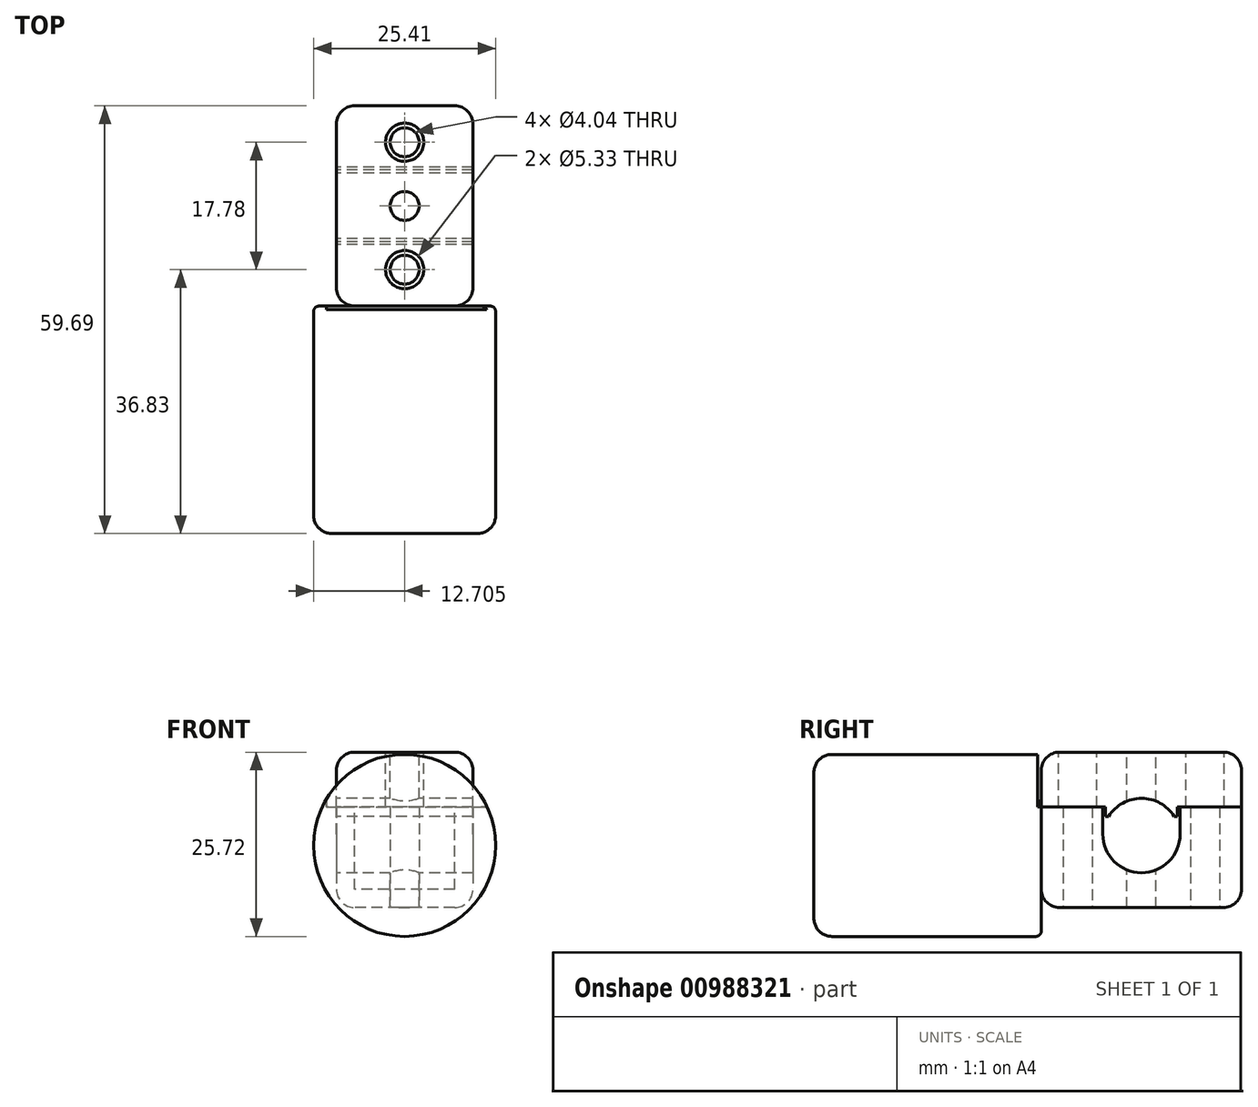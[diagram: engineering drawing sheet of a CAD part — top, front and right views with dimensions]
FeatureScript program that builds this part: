
annotation { "Feature Type Name" : "Feature", "Feature Type Description" : "" }
export const myFeature = defineFeature(function(context is Context, id is Id, definition is map)
    precondition{}
    {
        {
            var Q0;
            Q0=qCreatedBy(makeId("Right.planeOp"),FACE);
            var sketch = newSketch(context, id + "F0", { "sketchPlane" : qUnion([Q0])});
            skLineSegment(sketch, "E0", {"start": v(0, 11.43) * mm, "end": v(-13.97, 11.43) * mm});
            skLineSegment(sketch, "E1", {"start": v(-13.97, -10.27) * mm, "end": v(0, -10.27) * mm});
            skLineSegment(sketch, "E2", {"start": v(13.97, 3.81) * mm, "end": v(13.97, 11.43) * mm});
            skLineSegment(sketch, "E3", {"start": v(0, 11.43) * mm, "end": v(13.97, 11.43) * mm});
            skLineSegment(sketch, "E4", {"start": v(13.97, -10.27) * mm, "end": v(0, -10.27) * mm});
            skArc(sketch, "E5.trimOffspring", {"start": v(-5.4, 0) * mm, "mid": v(0, -5.4) * mm, "end": v(5.4, 0) * mm});
            skLineSegment(sketch, "E6", {"start": v(5.4, 0) * mm, "end": v(5.4, 3.78) * mm});
            skLineSegment(sketch, "E7", {"start": v(5.4, 3.78) * mm, "end": v(13.97, 3.78) * mm});
            skLineSegment(sketch, "E8", {"start": v(13.97, 3.78) * mm, "end": v(13.97, -10.27) * mm});
            skLineSegment(sketch, "E9", {"start": v(-13.97, 3.78) * mm, "end": v(-5.4, 3.78) * mm});
            skLineSegment(sketch, "E10", {"start": v(-5.4, 3.78) * mm, "end": v(-5.4, 0) * mm});
            skLineSegment(sketch, "E11", {"start": v(-13.97, -10.27) * mm, "end": v(-13.97, 3.78) * mm});
            skLineSegment(sketch, "E12", {"start": v(-13.97, 3.81) * mm, "end": v(-13.97, 11.43) * mm});
            skLineSegment(sketch, "E13.trimOffspring", {"start": v(-13.97, 3.81) * mm, "end": v(-5.02, 3.81) * mm});
            skLineSegment(sketch, "E14.left", {"start": v(5.02, 3.81) * mm, "end": v(5.02, 2.46) * mm});
            skLineSegment(sketch, "E15.left", {"start": v(-5.02, 3.81) * mm, "end": v(-5.02, 2.46) * mm});
            skLineSegment(sketch, "E16.trimOffspring", {"start": v(5.02, 3.81) * mm, "end": v(13.97, 3.81) * mm});
            skLineSegment(sketch, "E17", {"start": v(5.02, 2.46) * mm, "end": v(4.57, 2.46) * mm});
            skLineSegment(sketch, "E18", {"start": v(-5.02, 2.46) * mm, "end": v(-4.57, 2.46) * mm});
            skArc(sketch, "E19", {"start": v(4.57, 2.46) * mm, "mid": v(0, 4.98) * mm, "end": v(-4.57, 2.46) * mm});
            skSolve(sketch);
        }
        {
            var Q0;
            Q0=qSketchRegion(id+"F0",true);
            extrude(context, id + "F1", {"entities" : qUnion([Q0]), "depth" : 19.05 * mm, "offsetDistance" : 25.4 * mm});
        }
        {
            var Q0;
            Q0=makeQuery(id+"F1.opExtrude","SWEPT_FACE",FACE,{"disambiguationData":[OSD([sQuery(id+"F0.wireOp",EDGE,"E0"),sQuery(id+"F0.wireOp",EDGE,"E3")])]});
            var sketch = newSketch(context, id + "F2", { "sketchPlane" : qUnion([Q0])});
            skCircle(sketch, "E20", {"center": v(9.53, -8.9) * mm, "radius": 2.67 * mm});
            skPoint(sketch, "E20.centerSnap0", {"position": v(9.53, 13.97) * mm});
            skCircle(sketch, "E21", {"center": v(9.53, 8.9) * mm, "radius": 2.67 * mm});
            skCircle(sketch, "E22", {"center": v(9.53, 0) * mm, "radius": 2.02 * mm});
            skSolve(sketch);
        }
        {
            var Q0;
            Q0=qSketchRegion(id+"F2",true);
            extrude(context, id + "F3", {"entities" : qUnion([Q0]), "operationType" : NewBodyOperationType.REMOVE, "oppositeDirection" : true, "depth" : 25.4 * mm, "offsetDistance" : 25.4 * mm});
        }
        {
            var Q0;
            Q0=makeQuery(id+"F1.opExtrude","SWEPT_FACE",FACE,{"disambiguationData":[OSD([sQuery(id+"F0.wireOp",EDGE,"E1"),sQuery(id+"F0.wireOp",EDGE,"E4")])]});
            var sketch = newSketch(context, id + "F4", { "sketchPlane" : qUnion([Q0])});
            skSolve(sketch);
        }
        {
            var Q0;
            Q0=makeQuery(id+"F1.opExtrude","SWEPT_EDGE",EDGE,{"disambiguationData":[OSD([sQuery(id+"F0.wireOp",EDGE,"RtNWUVL0-efdT-tvqy-NiaK-mgzKuhDWmYlO"),sQuery(id+"F0.wireOp",EDGE,"E4")])]});
            var Q1;
            Q1=makeQuery(id+"F1.opExtrude","SWEPT_EDGE",EDGE,{"disambiguationData":[OSD([sQuery(id+"F0.wireOp",EDGE,"E2"),sQuery(id+"F0.wireOp",EDGE,"E3")])]});
            var Q2;
            Q2=makeQuery(id+"F1.opExtrude","CAP_EDGE",EDGE,{"disambiguationData":[OSD([sQuery(id+"F0.wireOp",EDGE,"E0"),sQuery(id+"F0.wireOp",EDGE,"E3")])],"isStart":true});
            var Q3;
            Q3=makeQuery(id+"F1.opExtrude","SWEPT_EDGE",EDGE,{"disambiguationData":[OSD([sQuery(id+"F0.wireOp",EDGE,"E0"),sQuery(id+"F0.wireOp",EDGE,"E12")])]});
            var Q4;
            Q4=makeQuery(id+"F1.opExtrude","CAP_EDGE",EDGE,{"disambiguationData":[OSD([sQuery(id+"F0.wireOp",EDGE,"E0"),sQuery(id+"F0.wireOp",EDGE,"E3")])],"isStart":false});
            var Q5;
            Q5=makeQuery(id+"F1.opExtrude","CAP_EDGE",EDGE,{"disambiguationData":[OSD([sQuery(id+"F0.wireOp",EDGE,"E1"),sQuery(id+"F0.wireOp",EDGE,"E4")])],"isStart":true});
            var Q6;
            Q6=makeQuery(id+"F1.opExtrude","SWEPT_EDGE",EDGE,{"disambiguationData":[OSD([sQuery(id+"F0.wireOp",EDGE,"E1"),sQuery(id+"F0.wireOp",EDGE,"E11")])]});
            var Q7;
            Q7=makeQuery(id+"F1.opExtrude","CAP_EDGE",EDGE,{"disambiguationData":[OSD([sQuery(id+"F0.wireOp",EDGE,"E11")])],"isStart":false});
            var Q8;
            Q8=makeQuery(id+"F1.opExtrude","CAP_EDGE",EDGE,{"disambiguationData":[OSD([sQuery(id+"F0.wireOp",EDGE,"E11")])],"isStart":true});
            var Q9;
            Q9=makeQuery(id+"F1.opExtrude","CAP_EDGE",EDGE,{"disambiguationData":[OSD([sQuery(id+"F0.wireOp",EDGE,"E8")])],"isStart":false});
            var Q10;
            Q10=makeQuery(id+"F1.opExtrude","CAP_EDGE",EDGE,{"disambiguationData":[OSD([sQuery(id+"F0.wireOp",EDGE,"E8")])],"isStart":true});
            var Q11;
            Q11=makeQuery(id+"F1.opExtrude","CAP_EDGE",EDGE,{"disambiguationData":[OSD([sQuery(id+"F0.wireOp",EDGE,"E2")])],"isStart":false});
            var Q12;
            Q12=makeQuery(id+"F1.opExtrude","CAP_EDGE",EDGE,{"disambiguationData":[OSD([sQuery(id+"F0.wireOp",EDGE,"E2")])],"isStart":true});
            var Q13;
            Q13=makeQuery(id+"F1.opExtrude","CAP_EDGE",EDGE,{"disambiguationData":[OSD([sQuery(id+"F0.wireOp",EDGE,"E12")])],"isStart":true});
            var Q14;
            Q14=makeQuery(id+"F1.opExtrude","CAP_EDGE",EDGE,{"disambiguationData":[OSD([sQuery(id+"F0.wireOp",EDGE,"E12")])],"isStart":false});
            var Q15;
            Q15=makeQuery(id+"F1.opExtrude","CAP_EDGE",EDGE,{"disambiguationData":[OSD([sQuery(id+"F0.wireOp",EDGE,"E1"),sQuery(id+"F0.wireOp",EDGE,"E4")])],"isStart":false});
            fillet(context, id + "F5", {"entities" : qUnion([Q0, Q1, Q2, Q3, Q4, Q5, Q6, Q7, Q8, Q9, Q10, Q11, Q12, Q13, Q14, Q15]), "radius" : 2.54 * mm, "tangentPropagation" : true, "allowEdgeOverflow" : false});
        }
        {
            var Q0;
            Q0=makeQuery(id+"F1.opExtrude","SWEPT_FACE",FACE,{"disambiguationData":[OSD([sQuery(id+"F0.wireOp",EDGE,"E11")])]});
            var sketch = newSketch(context, id + "F6", { "sketchPlane" : qUnion([Q0])});
            skPoint(sketch, "E23.centerSnap0", {"position": v(9.53, -7.73) * mm});
            skCircle(sketch, "E24", {"center": v(9.53, -1.59) * mm, "radius": 12.7 * mm});
            skSolve(sketch);
        }
        {
            var Q0;
            Q0 = qSketchRegion(id + "F6", true);
            extrude(context, id + "F7", {"entities" : qUnion([Q0]), "operationType" : NewBodyOperationType.ADD, "depth" : 31.75 * mm, "offsetDistance" : 25.4 * mm});
        }
        {
            var Q0;
            {var subQ1=sQuery(id+"F0.wireOp",EDGE,"E1");Q0=makeQuery(id+"F4.imprint","IMPRINT",FACE,{"disambiguationData":[TD([[makeQuery(id+"F4.imprint","IMPRINT",EDGE,{"derivedFrom":makeQuery(id+"F1.opExtrude","SWEPT_EDGE",EDGE,{"disambiguationData":[OSD([subQ1,sQuery(id+"F0.wireOp",EDGE,"E11")])]})}),1.0]])]});}
            var sketch = newSketch(context, id + "F8", { "sketchPlane" : qUnion([Q0])});
            skCircle(sketch, "E25.0", {"center": v(9.53, -8.9) * mm, "radius": 2.67 * mm});
            skCircle(sketch, "E26", {"center": v(9.53, -8.9) * mm, "radius": 2.02 * mm});
            skCircle(sketch, "E27.0", {"center": v(9.53, 8.9) * mm, "radius": 2.67 * mm});
            skCircle(sketch, "E28", {"center": v(9.53, 8.9) * mm, "radius": 2.02 * mm});
            skSolve(sketch);
        }
        {
            var Q0;
            Q0 = qSketchRegion(id + "F8", true);
            var Q1;
            Q1=makeQuery(id+"F1.opExtrude","SWEPT_FACE",FACE,{"disambiguationData":[OSD([sQuery(id+"F0.wireOp",EDGE,"E9")])]});
            extrude(context, id + "F9", {"entities" : qUnion([Q0]), "operationType" : NewBodyOperationType.ADD, "endBound" : BoundingType.UP_TO_SURFACE, "oppositeDirection" : true, "depth" : 25.4 * mm, "endBoundEntityFace" : qUnion([Q1]), "offsetDistance" : 25.4 * mm});
        }
        {
            var Q0;
            Q0=makeQuery(id+"F1.opExtrude","SWEPT_FACE",FACE,{"disambiguationData":[OSD([sQuery(id+"F0.wireOp",EDGE,"E9")])]});
            var sketch = newSketch(context, id + "F10", { "sketchPlane" : qUnion([Q0])});
            skLineSegment(sketch, "E29.bottom", {"start": v(-1.4, -14.48) * mm, "end": v(35.1, -14.48) * mm});
            skLineSegment(sketch, "E29.top", {"start": v(-1.4, -13.97) * mm, "end": v(35.1, -13.97) * mm});
            skLineSegment(sketch, "E29.left", {"start": v(-1.4, -14.48) * mm, "end": v(-1.4, -13.97) * mm});
            skLineSegment(sketch, "E29.right", {"start": v(35.1, -14.48) * mm, "end": v(35.1, -13.97) * mm});
            skSolve(sketch);
        }
        {
            var Q0;
            Q0 = qSketchRegion(id + "F10", true);
            extrude(context, id + "F11", {"entities" : qUnion([Q0]), "operationType" : NewBodyOperationType.REMOVE, "depth" : 25.4 * mm, "offsetDistance" : 25.4 * mm});
        }
        {
            var Q0;
            Q0=makeQuery(id+"F7.opExtrude","CAP_EDGE",EDGE,{"disambiguationData":[OSD([sQuery(id+"F6.wireOp",EDGE,"E24")])],"isStart":false});
            var Q1;
            {var subQ0=sQuery(id+"F0.wireOp",EDGE,"E11");Q1=makeQuery(id+"F5.opFillet","BLEND_EDGE",EDGE,{"blendedFrom":[makeQuery(id+"F1.opExtrude","CAP_EDGE",EDGE,{"disambiguationData":[OSD([subQ0])],"isStart":true}),makeQuery(id+"F1.opExtrude","SWEPT_FACE",FACE,{"disambiguationData":[OSD([subQ0])]})],"blendedInto":[makeQuery(id+"F1.opExtrude","SWEPT_FACE",FACE,{"disambiguationData":[OSD([subQ0])]})]});}
            fillet(context, id + "F12", {"entities" : qUnion([Q0, Q1]), "radius" : 2.54 * mm, "tangentPropagation" : true, "allowEdgeOverflow" : false});
        }
        {
            var Q0;
            Q0=makeQuery(id+"F7.opExtrude","CAP_EDGE",EDGE,{"disambiguationData":[OSD([sQuery(id+"F6.wireOp",EDGE,"E24")])],"isStart":true});
            fillet(context, id + "F13", {"entities" : qUnion([Q0]), "radius" : 0.76 * mm, "tangentPropagation" : true, "allowEdgeOverflow" : false});
        }
    });
